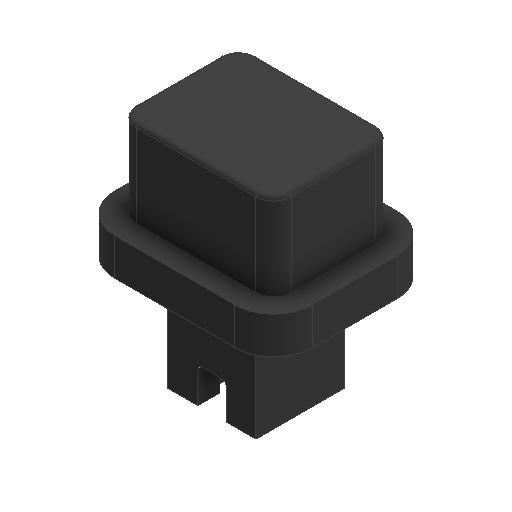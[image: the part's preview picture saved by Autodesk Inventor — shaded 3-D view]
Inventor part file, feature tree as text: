
AUTODESK INVENTOR PART (.ipt)
format: ipt  version: 2025 (Build 290162000, 162)  size: 241,664 bytes
history: native  units: mm
features: extrude x6, sketch x6, fillet x5, mirror x1, plane x1
ambient origin geometry x8: Origin, YZ Plane, XZ Plane, XY Plane, X Axis, Y Axis, Z Axis, Center Point
bodies: Solid1 (feature_tree)
feature tree (19):
  extrude  "Extrusion1"  Depth=6.0mm TaperAngle=0.0deg
  extrude  "Extrusion2"  Depth=2.8mm TaperAngle=0.0deg
  extrude  "Extrusion3"  Depth=2.0mm
  extrude  "Extrusion4"  Depth=0.1mm
  mirror  "Mirror1"
  extrude  "Extrusion5"  Depth=0.14mm
  fillet  "Fillet1"  [1 undecoded]
  fillet  "Fillet2"  Radius=6.8mm
  extrude  "Extrusion6"  Depth=7.0mm TaperAngle=0.0deg
  fillet  "Fillet3"  Radius=1.0mm
  fillet  "Fillet4"  Radius=0.2mm
  fillet  "Fillet5"  Radius=1.2mm
  sketch  "Sketch1"  dims[d0=5.0mm d1=6.0mm d2=0.0mm]
  sketch  "Sketch2"  dims[d3=2.5mm d4=2.8mm d5=0.0mm]
  sketch  "Sketch3"  dims[d6=1.6mm d7=2.0mm]
  sketch  "Sketch4"  dims[d8=0.0mm d9=0.0mm d13=0.1mm]
  plane  "Work Plane1"
  sketch  "Sketch5"  dims[d14=1.9mm d15=0.14mm d16=0.0mm d17=0.0mm d18=6.8mm]
  sketch  "Sketch6"  dims[d19=8.8mm d20=7.0mm d21=0.0mm d22=1.0mm d23=0.2mm d24=1.2mm d25=2.1mm d26=0.0mm d27=0.6mm d28=30.0deg d29=0.105946mm d30=1.9mm d31=0.2mm d32=0.2mm]
note: 1 required parameter value undecoded (feature->parameter linkage not recoverable at this tier; creation-order binding heuristic only, values carry confidence <= 0.55)
